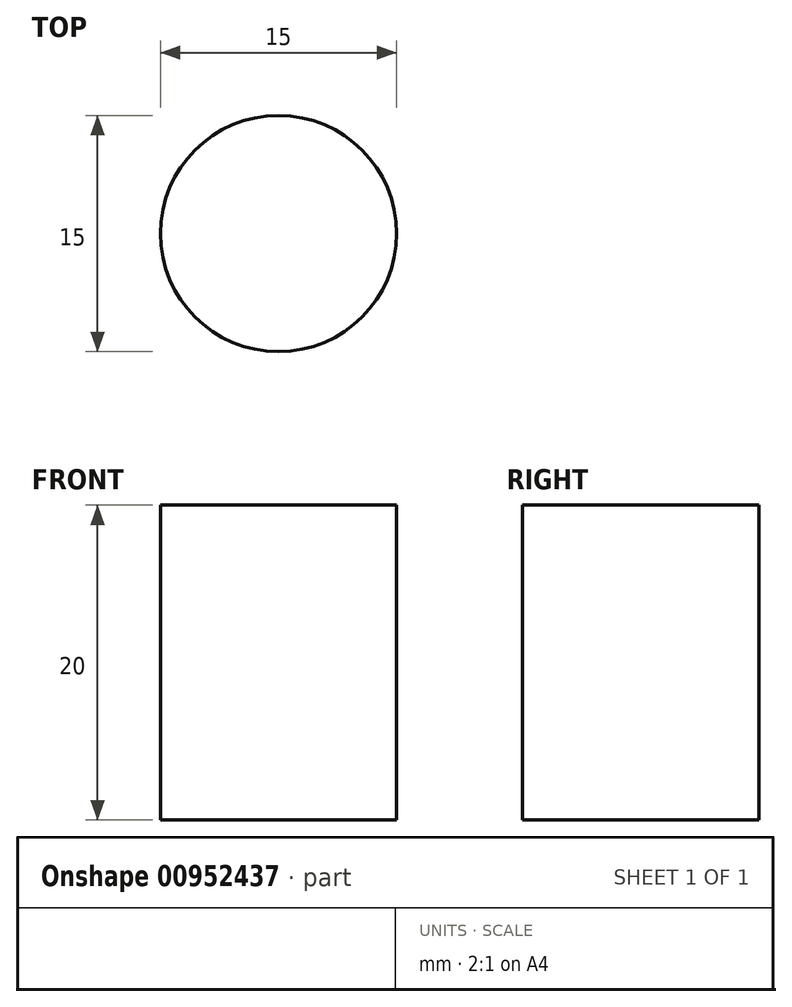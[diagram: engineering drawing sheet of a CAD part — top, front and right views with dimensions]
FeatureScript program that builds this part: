
annotation { "Feature Type Name" : "Feature", "Feature Type Description" : "" }
export const myFeature = defineFeature(function(context is Context, id is Id, definition is map)
    precondition{}
    {
        {
            var Q0;
            Q0=qCreatedBy(makeId("Top.planeOp"),FACE);
            var sketch = newSketch(context, id + "F0", { "sketchPlane" : qUnion([Q0])});
            skCircle(sketch, "E0", {"center": v(0, 0) * mm, "radius": 7.5 * mm});
            skSolve(sketch);
        }
        {
            var Q0;
            Q0=makeQuery(id+"F0.imprint","IMPRINT",FACE,{"disambiguationData":[TD([[makeQuery(id+"F0.imprint","IMPRINT",EDGE,{"derivedFrom":sQuery(id+"F0.wireOp",EDGE,"E0")}),1.0]])]});
            extrude(context, id + "F1", {"entities" : qUnion([Q0]), "depth" : 20 * mm, "offsetDistance" : 25 * mm});
        }
    });
